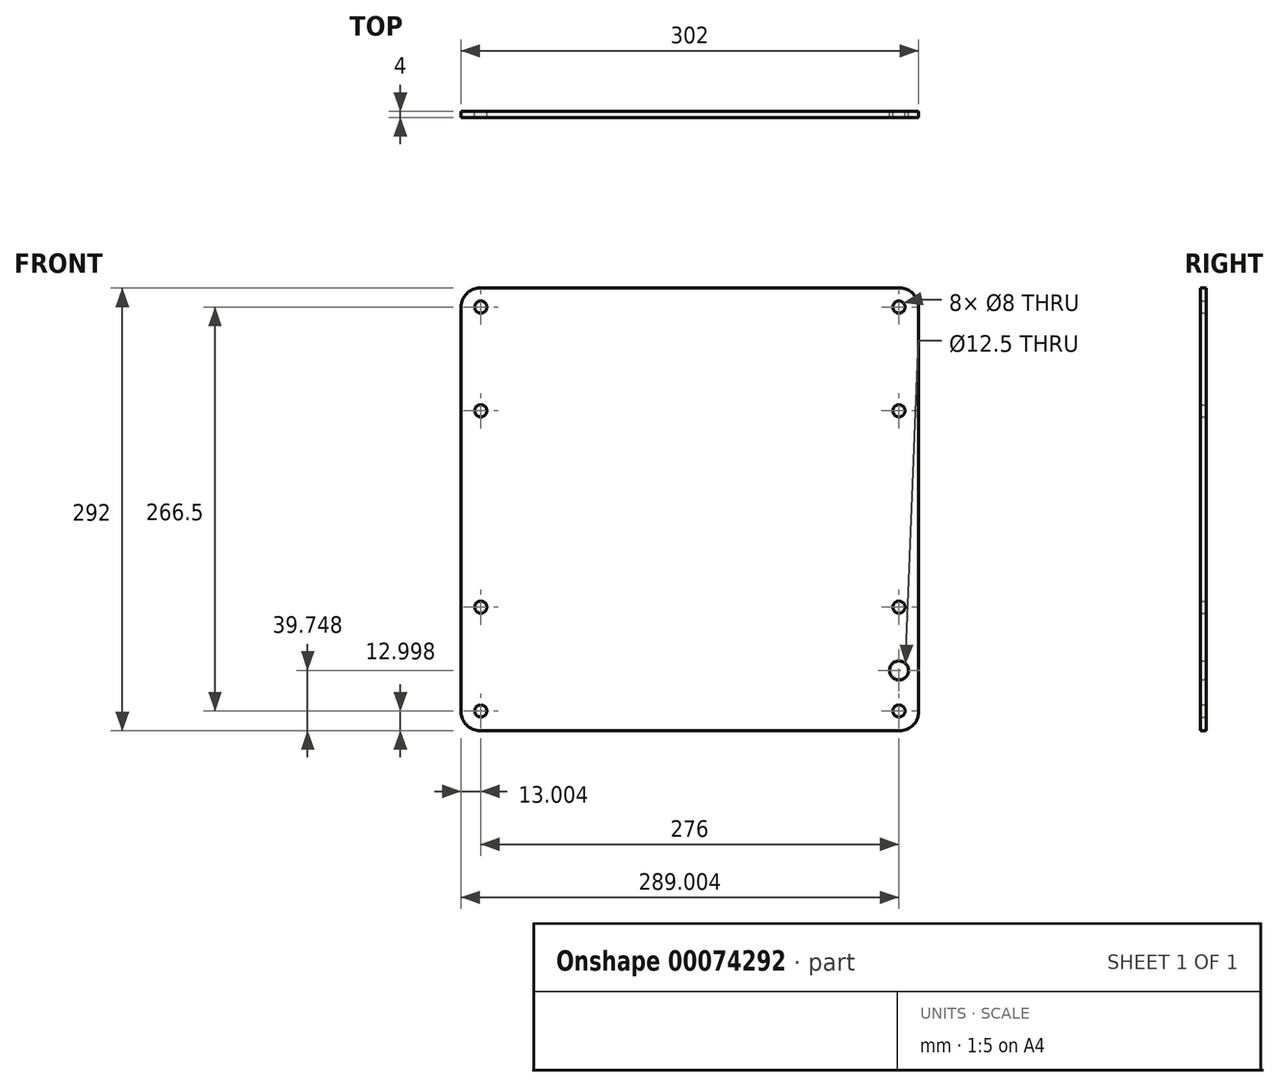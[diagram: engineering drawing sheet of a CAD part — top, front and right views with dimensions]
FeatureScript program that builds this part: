
annotation { "Feature Type Name" : "Feature", "Feature Type Description" : "" }
export const myFeature = defineFeature(function(context is Context, id is Id, definition is map)
    precondition{}
    {
        {
            var Q0;
            Q0=qCreatedBy(makeId("Front.planeOp"),FACE);
            var sketch = newSketch(context, id + "F0", { "sketchPlane" : qUnion([Q0])});
            skLineSegment(sketch, "E0.bottom", {"start": v(-155.83, -205.31) * mm, "end": v(146.17, -205.31) * mm});
            skLineSegment(sketch, "E0.top", {"start": v(-155.83, 86.69) * mm, "end": v(146.17, 86.69) * mm});
            skLineSegment(sketch, "E0.left", {"start": v(-155.83, -205.31) * mm, "end": v(-155.83, 86.69) * mm});
            skLineSegment(sketch, "E0.right", {"start": v(146.17, -205.31) * mm, "end": v(146.17, 86.69) * mm});
            skSolve(sketch);
        }
        {
            var Q0;
            Q0=makeQuery(id+"F0.imprint","IMPRINT",FACE,{"disambiguationData":[TD([[makeQuery(id+"F0.imprint","IMPRINT",EDGE,{"derivedFrom":sQuery(id+"F0.wireOp",EDGE,"E0.bottom")}),1.0]])]});
            extrude(context, id + "F1", {"entities" : qUnion([Q0]), "depth" : 4 * mm});
        }
        {
            var Q0;
            Q0=makeQuery(id+"F1.opExtrude","CAP_FACE",FACE,{"disambiguationData":[OSD([sQuery(id+"F0.wireOp",EDGE,"E0.bottom"),sQuery(id+"F0.wireOp",EDGE,"E0.top"),sQuery(id+"F0.wireOp",EDGE,"E0.left"),sQuery(id+"F0.wireOp",EDGE,"E0.right")])],"isStart":true});
            var sketch = newSketch(context, id + "F2", { "sketchPlane" : qUnion([Q0])});
            skCircle(sketch, "E1", {"center": v(-133.17, -192.31) * mm, "radius": 4 * mm});
            skCircle(sketch, "E2", {"center": v(-133.17, -123.81) * mm, "radius": 4 * mm});
            skCircle(sketch, "E3", {"center": v(-133.17, 5.69) * mm, "radius": 4 * mm});
            skCircle(sketch, "E4", {"center": v(-133.17, 74.19) * mm, "radius": 4 * mm});
            skCircle(sketch, "E5", {"center": v(142.83, -192.31) * mm, "radius": 4 * mm});
            skCircle(sketch, "E6", {"center": v(142.83, -123.81) * mm, "radius": 4 * mm});
            skCircle(sketch, "E7", {"center": v(142.83, 5.69) * mm, "radius": 4 * mm});
            skCircle(sketch, "E8", {"center": v(142.83, 74.19) * mm, "radius": 4 * mm});
            skCircle(sketch, "E9", {"center": v(-133.17, -165.56) * mm, "radius": 6.25 * mm});
            skSolve(sketch);
        }
        {
            var Q0;
            Q0 = qSketchRegion(id + "F2", true);
            extrude(context, id + "F3", {"entities" : qUnion([Q0]), "operationType" : NewBodyOperationType.REMOVE, "oppositeDirection" : true, "depth" : 25 * mm});
        }
        {
            var Q0;
            Q0=makeQuery(id+"F1.opExtrude","SWEPT_EDGE",EDGE,{"disambiguationData":[OSD([sQuery(id+"F0.wireOp",EDGE,"E0.top"),sQuery(id+"F0.wireOp",EDGE,"E0.right")])]});
            var Q1;
            Q1=makeQuery(id+"F1.opExtrude","SWEPT_EDGE",EDGE,{"disambiguationData":[OSD([sQuery(id+"F0.wireOp",EDGE,"E0.bottom"),sQuery(id+"F0.wireOp",EDGE,"E0.right")])]});
            var Q2;
            Q2=makeQuery(id+"F1.opExtrude","SWEPT_EDGE",EDGE,{"disambiguationData":[OSD([sQuery(id+"F0.wireOp",EDGE,"E0.bottom"),sQuery(id+"F0.wireOp",EDGE,"E0.left")])]});
            var Q3;
            Q3=makeQuery(id+"F1.opExtrude","SWEPT_EDGE",EDGE,{"disambiguationData":[OSD([sQuery(id+"F0.wireOp",EDGE,"E0.top"),sQuery(id+"F0.wireOp",EDGE,"E0.left")])]});
            fillet(context, id + "F4", {"entities" : qUnion([Q0, Q1, Q2, Q3]), "radius" : 12.5 * mm, "tangentPropagation" : true, "allowEdgeOverflow" : false});
        }
    });
